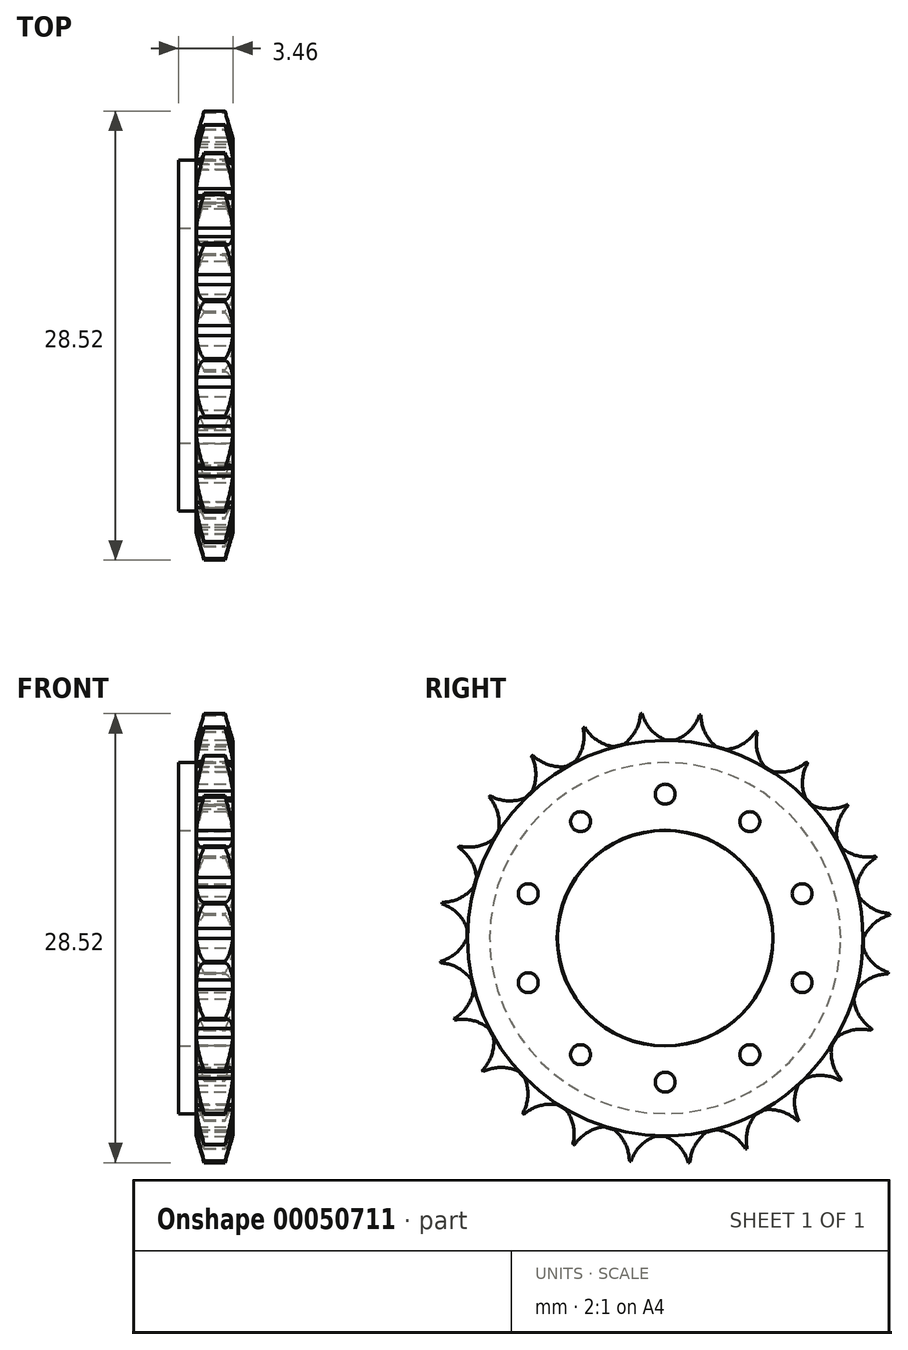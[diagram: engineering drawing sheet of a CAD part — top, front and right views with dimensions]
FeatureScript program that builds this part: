
annotation { "Feature Type Name" : "Feature", "Feature Type Description" : "" }
export const myFeature = defineFeature(function(context is Context, id is Id, definition is map)
    precondition{}
    {
        {
            var Q0;
            Q0=qCreatedBy(makeId("Right.planeOp"),FACE);
            var sketch = newSketch(context, id + "F0", { "sketchPlane" : qUnion([Q0])});
            skCircle(sketch, "E0", {"center": v(0, 0) * mm, "radius": 14.34 * mm});
            skCircle(sketch, "E1", {"center": v(0, 0) * mm, "radius": 6.86 * mm});
            skSolve(sketch);
        }
        {
            var Q0;
            Q0 = qSketchRegion(id + "F0", true);
            extrude(context, id + "F1", {"entities" : qUnion([Q0]), "flatOperationType" : FlatOperationType.REMOVE, "depth" : 2.34 * mm, "offsetDistance" : 25.4 * mm, "domain" : OperationDomain.MODEL});
        }
        {
            var Q0;
            Q0=makeQuery(id+"F1.opExtrude","CAP_EDGE",EDGE,{"disambiguationData":[OSD([sQuery(id+"F0.wireOp",EDGE,"E0")])],"isStart":false});
            var Q1;
            Q1=makeQuery(id+"F1.opExtrude","CAP_EDGE",EDGE,{"disambiguationData":[OSD([sQuery(id+"F0.wireOp",EDGE,"E0")])],"isStart":true});
            chamfer(context, id + "F2", {"entities" : qUnion([Q0, Q1]), "chamferType" : ChamferType.TWO_OFFSETS, "width1" : 1.78 * mm, "oppositeDirection" : false, "width2" : 0.5 * mm, "tangentPropagation" : true});
        }
        {
            var Q0;
            Q0=makeQuery(id+"F1.opExtrude","CAP_FACE",FACE,{"disambiguationData":[OSD([sQuery(id+"F0.wireOp",EDGE,"E0"),sQuery(id+"F0.wireOp",EDGE,"E1")])],"isStart":false});
            var sketch = newSketch(context, id + "F3", { "sketchPlane" : qUnion([Q0])});
            skCircle(sketch, "E2", {"center": v(0, 0) * mm, "radius": 12.6 * mm});
            skArc(sketch, "E3", {"start": v(-1.47, 14.28) * mm, "mid": v(-0.9, 13.23) * mm, "end": v(0.08, 12.56) * mm});
            skArc(sketch, "E4.MirrorCS", {"start": v(-1.57, 14.27) * mm, "mid": v(-1.9, 13.13) * mm, "end": v(-2.72, 12.26) * mm});
            skArc(sketch, "E5.1.0", {"start": v(-5.21, 13.38) * mm, "mid": v(-5.24, 12.19) * mm, "end": v(-5.8, 11.14) * mm});
            skArc(sketch, "E5.1.1", {"start": v(-5.12, 13.41) * mm, "mid": v(-4.3, 12.55) * mm, "end": v(-3.17, 12.15) * mm});
            skArc(sketch, "E5.2.0", {"start": v(-8.5, 11.57) * mm, "mid": v(-8.21, 10.42) * mm, "end": v(-8.49, 9.26) * mm});
            skArc(sketch, "E5.2.1", {"start": v(-8.41, 11.63) * mm, "mid": v(-7.4, 11) * mm, "end": v(-6.21, 10.92) * mm});
            skArc(sketch, "E5.3.0", {"start": v(-11.2, 8.98) * mm, "mid": v(-10.63, 7.93) * mm, "end": v(-10.6, 6.74) * mm});
            skArc(sketch, "E5.3.1", {"start": v(-11.14, 9.06) * mm, "mid": v(-10, 8.72) * mm, "end": v(-8.82, 8.94) * mm});
            skArc(sketch, "E5.4.0", {"start": v(-13.14, 5.77) * mm, "mid": v(-12.32, 4.91) * mm, "end": v(-11.98, 3.77) * mm});
            skArc(sketch, "E5.4.1", {"start": v(-13.1, 5.87) * mm, "mid": v(-11.91, 5.84) * mm, "end": v(-10.84, 6.35) * mm});
            skArc(sketch, "E5.5.0", {"start": v(-14.2, 2.18) * mm, "mid": v(-13.17, 1.56) * mm, "end": v(-12.55, 0.54) * mm});
            skArc(sketch, "E5.5.1", {"start": v(-14.17, 2.28) * mm, "mid": v(-13.02, 2.55) * mm, "end": v(-12.11, 3.33) * mm});
            skArc(sketch, "E5.6.0", {"start": v(-14.27, -1.57) * mm, "mid": v(-13.13, -1.9) * mm, "end": v(-12.26, -2.72) * mm});
            skArc(sketch, "E5.6.1", {"start": v(-14.28, -1.47) * mm, "mid": v(-13.23, -0.9) * mm, "end": v(-12.56, 0.08) * mm});
            skArc(sketch, "E5.7.0", {"start": v(-13.38, -5.21) * mm, "mid": v(-12.19, -5.24) * mm, "end": v(-11.14, -5.8) * mm});
            skArc(sketch, "E5.7.1", {"start": v(-13.41, -5.12) * mm, "mid": v(-12.55, -4.3) * mm, "end": v(-12.15, -3.17) * mm});
            skArc(sketch, "E5.8.0", {"start": v(-11.57, -8.5) * mm, "mid": v(-10.42, -8.21) * mm, "end": v(-9.26, -8.49) * mm});
            skArc(sketch, "E5.8.1", {"start": v(-11.63, -8.41) * mm, "mid": v(-11, -7.4) * mm, "end": v(-10.92, -6.21) * mm});
            skArc(sketch, "E5.9.0", {"start": v(-8.98, -11.2) * mm, "mid": v(-7.93, -10.63) * mm, "end": v(-6.74, -10.6) * mm});
            skArc(sketch, "E5.9.1", {"start": v(-9.06, -11.14) * mm, "mid": v(-8.72, -10) * mm, "end": v(-8.94, -8.82) * mm});
            skArc(sketch, "E5.10.0", {"start": v(-5.77, -13.14) * mm, "mid": v(-4.91, -12.32) * mm, "end": v(-3.77, -11.98) * mm});
            skArc(sketch, "E5.10.1", {"start": v(-5.87, -13.1) * mm, "mid": v(-5.84, -11.91) * mm, "end": v(-6.35, -10.84) * mm});
            skArc(sketch, "E5.11.0", {"start": v(-2.18, -14.2) * mm, "mid": v(-1.56, -13.17) * mm, "end": v(-0.54, -12.55) * mm});
            skArc(sketch, "E5.11.1", {"start": v(-2.28, -14.17) * mm, "mid": v(-2.55, -13.02) * mm, "end": v(-3.33, -12.11) * mm});
            skArc(sketch, "E5.12.0", {"start": v(1.57, -14.27) * mm, "mid": v(1.9, -13.13) * mm, "end": v(2.72, -12.26) * mm});
            skArc(sketch, "E5.12.1", {"start": v(1.47, -14.28) * mm, "mid": v(0.9, -13.23) * mm, "end": v(-0.08, -12.56) * mm});
            skArc(sketch, "E5.13.0", {"start": v(5.21, -13.38) * mm, "mid": v(5.24, -12.19) * mm, "end": v(5.8, -11.14) * mm});
            skArc(sketch, "E5.13.1", {"start": v(5.12, -13.41) * mm, "mid": v(4.3, -12.55) * mm, "end": v(3.17, -12.15) * mm});
            skArc(sketch, "E5.14.0", {"start": v(8.5, -11.57) * mm, "mid": v(8.21, -10.42) * mm, "end": v(8.49, -9.26) * mm});
            skArc(sketch, "E5.14.1", {"start": v(8.41, -11.63) * mm, "mid": v(7.4, -11) * mm, "end": v(6.21, -10.92) * mm});
            skArc(sketch, "E5.15.0", {"start": v(11.2, -8.98) * mm, "mid": v(10.63, -7.93) * mm, "end": v(10.6, -6.74) * mm});
            skArc(sketch, "E5.15.1", {"start": v(11.14, -9.06) * mm, "mid": v(10, -8.72) * mm, "end": v(8.82, -8.94) * mm});
            skArc(sketch, "E5.16.0", {"start": v(13.14, -5.77) * mm, "mid": v(12.32, -4.91) * mm, "end": v(11.98, -3.77) * mm});
            skArc(sketch, "E5.16.1", {"start": v(13.1, -5.87) * mm, "mid": v(11.91, -5.84) * mm, "end": v(10.84, -6.35) * mm});
            skArc(sketch, "E5.17.0", {"start": v(14.2, -2.18) * mm, "mid": v(13.17, -1.56) * mm, "end": v(12.55, -0.54) * mm});
            skArc(sketch, "E5.17.1", {"start": v(14.17, -2.28) * mm, "mid": v(13.02, -2.55) * mm, "end": v(12.11, -3.33) * mm});
            skArc(sketch, "E5.18.0", {"start": v(14.27, 1.57) * mm, "mid": v(13.13, 1.9) * mm, "end": v(12.26, 2.72) * mm});
            skArc(sketch, "E5.18.1", {"start": v(14.28, 1.47) * mm, "mid": v(13.23, 0.9) * mm, "end": v(12.56, -0.08) * mm});
            skArc(sketch, "E5.19.0", {"start": v(13.38, 5.21) * mm, "mid": v(12.19, 5.24) * mm, "end": v(11.14, 5.8) * mm});
            skArc(sketch, "E5.19.1", {"start": v(13.41, 5.12) * mm, "mid": v(12.55, 4.3) * mm, "end": v(12.15, 3.17) * mm});
            skArc(sketch, "E5.20.0", {"start": v(11.57, 8.5) * mm, "mid": v(10.42, 8.21) * mm, "end": v(9.26, 8.49) * mm});
            skArc(sketch, "E5.20.1", {"start": v(11.63, 8.41) * mm, "mid": v(11, 7.4) * mm, "end": v(10.92, 6.21) * mm});
            skArc(sketch, "E5.21.0", {"start": v(8.98, 11.2) * mm, "mid": v(7.93, 10.63) * mm, "end": v(6.74, 10.6) * mm});
            skArc(sketch, "E5.21.1", {"start": v(9.06, 11.14) * mm, "mid": v(8.72, 10) * mm, "end": v(8.94, 8.82) * mm});
            skArc(sketch, "E5.22.0", {"start": v(5.77, 13.14) * mm, "mid": v(4.91, 12.32) * mm, "end": v(3.77, 11.98) * mm});
            skArc(sketch, "E5.22.1", {"start": v(5.87, 13.1) * mm, "mid": v(5.84, 11.91) * mm, "end": v(6.35, 10.84) * mm});
            skArc(sketch, "E5.23.0", {"start": v(2.18, 14.2) * mm, "mid": v(1.56, 13.17) * mm, "end": v(0.54, 12.55) * mm});
            skArc(sketch, "E5.23.1", {"start": v(2.28, 14.17) * mm, "mid": v(2.55, 13.02) * mm, "end": v(3.33, 12.11) * mm});
            skCircle(sketch, "E6", {"center": v(0, 0) * mm, "radius": 14.36 * mm});
            skSolve(sketch);
        }
        {
            var Q0;
            {var subQ0=sQuery(id+"F3.wireOp",EDGE,"E5.18.0");var subQ1=sQuery(id+"F3.wireOp",EDGE,"E2");var subQ2=makeQuery(id+"F3.imprint","INTERSECT",VERTEX,{"derivedFrom":[subQ1,subQ0]});Q0=makeQuery(id+"F3.imprint","IMPRINT",FACE,{"disambiguationData":[TD([[makeQuery(id+"F3.imprint","IMPRINT",EDGE,{"disambiguationData":[TD([[subQ2,-1.0]])],"derivedFrom":subQ1}),-1.0]])]});}
            var Q1;
            {var subQ0=sQuery(id+"F3.wireOp",EDGE,"E5.19.0");var subQ1=sQuery(id+"F3.wireOp",EDGE,"E2");var subQ2=makeQuery(id+"F3.imprint","INTERSECT",VERTEX,{"derivedFrom":[subQ1,subQ0]});Q1=makeQuery(id+"F3.imprint","IMPRINT",FACE,{"disambiguationData":[TD([[makeQuery(id+"F3.imprint","IMPRINT",EDGE,{"disambiguationData":[TD([[subQ2,-1.0]])],"derivedFrom":subQ1}),-1.0]])]});}
            var Q2;
            {var subQ0=sQuery(id+"F3.wireOp",EDGE,"E5.20.0");var subQ1=sQuery(id+"F3.wireOp",EDGE,"E2");var subQ2=makeQuery(id+"F3.imprint","INTERSECT",VERTEX,{"derivedFrom":[subQ1,subQ0]});Q2=makeQuery(id+"F3.imprint","IMPRINT",FACE,{"disambiguationData":[TD([[makeQuery(id+"F3.imprint","IMPRINT",EDGE,{"disambiguationData":[TD([[subQ2,-1.0]])],"derivedFrom":subQ1}),-1.0]])]});}
            var Q3;
            {var subQ0=sQuery(id+"F3.wireOp",EDGE,"E5.21.0");var subQ1=sQuery(id+"F3.wireOp",EDGE,"E2");var subQ2=makeQuery(id+"F3.imprint","INTERSECT",VERTEX,{"derivedFrom":[subQ1,subQ0]});Q3=makeQuery(id+"F3.imprint","IMPRINT",FACE,{"disambiguationData":[TD([[makeQuery(id+"F3.imprint","IMPRINT",EDGE,{"disambiguationData":[TD([[subQ2,-1.0]])],"derivedFrom":subQ1}),-1.0]])]});}
            var Q4;
            {var subQ0=sQuery(id+"F3.wireOp",EDGE,"E5.22.0");var subQ1=sQuery(id+"F3.wireOp",EDGE,"E2");var subQ2=makeQuery(id+"F3.imprint","INTERSECT",VERTEX,{"derivedFrom":[subQ1,subQ0]});Q4=makeQuery(id+"F3.imprint","IMPRINT",FACE,{"disambiguationData":[TD([[makeQuery(id+"F3.imprint","IMPRINT",EDGE,{"disambiguationData":[TD([[subQ2,-1.0]])],"derivedFrom":subQ1}),-1.0]])]});}
            var Q5;
            {var subQ0=sQuery(id+"F3.wireOp",EDGE,"E5.23.0");var subQ1=sQuery(id+"F3.wireOp",EDGE,"E2");var subQ2=makeQuery(id+"F3.imprint","INTERSECT",VERTEX,{"derivedFrom":[subQ1,subQ0]});Q5=makeQuery(id+"F3.imprint","IMPRINT",FACE,{"disambiguationData":[TD([[makeQuery(id+"F3.imprint","IMPRINT",EDGE,{"disambiguationData":[TD([[subQ2,-1.0]])],"derivedFrom":subQ1}),-1.0]])]});}
            var Q6;
            {var subQ0=sQuery(id+"F3.wireOp",EDGE,"E5.1.0");var subQ1=sQuery(id+"F3.wireOp",EDGE,"E2");var subQ2=makeQuery(id+"F3.imprint","INTERSECT",VERTEX,{"derivedFrom":[subQ1,subQ0]});Q6=makeQuery(id+"F3.imprint","IMPRINT",FACE,{"disambiguationData":[TD([[makeQuery(id+"F3.imprint","IMPRINT",EDGE,{"disambiguationData":[TD([[subQ2,-1.0]])],"derivedFrom":subQ1}),-1.0]])]});}
            var Q7;
            {var subQ0=sQuery(id+"F3.wireOp",EDGE,"E5.2.0");var subQ1=sQuery(id+"F3.wireOp",EDGE,"E2");var subQ2=makeQuery(id+"F3.imprint","INTERSECT",VERTEX,{"derivedFrom":[subQ1,subQ0]});Q7=makeQuery(id+"F3.imprint","IMPRINT",FACE,{"disambiguationData":[TD([[makeQuery(id+"F3.imprint","IMPRINT",EDGE,{"disambiguationData":[TD([[subQ2,-1.0]])],"derivedFrom":subQ1}),-1.0]])]});}
            var Q8;
            {var subQ0=sQuery(id+"F3.wireOp",EDGE,"E5.3.0");var subQ1=sQuery(id+"F3.wireOp",EDGE,"E2");var subQ2=makeQuery(id+"F3.imprint","INTERSECT",VERTEX,{"derivedFrom":[subQ1,subQ0]});Q8=makeQuery(id+"F3.imprint","IMPRINT",FACE,{"disambiguationData":[TD([[makeQuery(id+"F3.imprint","IMPRINT",EDGE,{"disambiguationData":[TD([[subQ2,-1.0]])],"derivedFrom":subQ1}),-1.0]])]});}
            var Q9;
            {var subQ0=sQuery(id+"F3.wireOp",EDGE,"E5.4.0");var subQ1=sQuery(id+"F3.wireOp",EDGE,"E2");var subQ2=makeQuery(id+"F3.imprint","INTERSECT",VERTEX,{"derivedFrom":[subQ1,subQ0]});Q9=makeQuery(id+"F3.imprint","IMPRINT",FACE,{"disambiguationData":[TD([[makeQuery(id+"F3.imprint","IMPRINT",EDGE,{"disambiguationData":[TD([[subQ2,-1.0]])],"derivedFrom":subQ1}),-1.0]])]});}
            var Q10;
            {var subQ0=sQuery(id+"F3.wireOp",EDGE,"E5.5.0");var subQ1=sQuery(id+"F3.wireOp",EDGE,"E2");var subQ2=makeQuery(id+"F3.imprint","INTERSECT",VERTEX,{"derivedFrom":[subQ1,subQ0]});Q10=makeQuery(id+"F3.imprint","IMPRINT",FACE,{"disambiguationData":[TD([[makeQuery(id+"F3.imprint","IMPRINT",EDGE,{"disambiguationData":[TD([[subQ2,-1.0]])],"derivedFrom":subQ1}),-1.0]])]});}
            var Q11;
            {var subQ0=sQuery(id+"F3.wireOp",EDGE,"E5.6.0");var subQ1=sQuery(id+"F3.wireOp",EDGE,"E2");var subQ2=makeQuery(id+"F3.imprint","INTERSECT",VERTEX,{"derivedFrom":[subQ1,subQ0]});Q11=makeQuery(id+"F3.imprint","IMPRINT",FACE,{"disambiguationData":[TD([[makeQuery(id+"F3.imprint","IMPRINT",EDGE,{"disambiguationData":[TD([[subQ2,-1.0]])],"derivedFrom":subQ1}),-1.0]])]});}
            var Q12;
            {var subQ0=sQuery(id+"F3.wireOp",EDGE,"E5.7.0");var subQ1=sQuery(id+"F3.wireOp",EDGE,"E2");var subQ2=makeQuery(id+"F3.imprint","INTERSECT",VERTEX,{"derivedFrom":[subQ1,subQ0]});Q12=makeQuery(id+"F3.imprint","IMPRINT",FACE,{"disambiguationData":[TD([[makeQuery(id+"F3.imprint","IMPRINT",EDGE,{"disambiguationData":[TD([[subQ2,-1.0]])],"derivedFrom":subQ1}),-1.0]])]});}
            var Q13;
            {var subQ0=sQuery(id+"F3.wireOp",EDGE,"E5.8.0");var subQ1=sQuery(id+"F3.wireOp",EDGE,"E2");var subQ2=makeQuery(id+"F3.imprint","INTERSECT",VERTEX,{"derivedFrom":[subQ1,subQ0]});Q13=makeQuery(id+"F3.imprint","IMPRINT",FACE,{"disambiguationData":[TD([[makeQuery(id+"F3.imprint","IMPRINT",EDGE,{"disambiguationData":[TD([[subQ2,-1.0]])],"derivedFrom":subQ1}),-1.0]])]});}
            var Q14;
            {var subQ0=sQuery(id+"F3.wireOp",EDGE,"E5.9.0");var subQ1=sQuery(id+"F3.wireOp",EDGE,"E2");var subQ2=makeQuery(id+"F3.imprint","INTERSECT",VERTEX,{"derivedFrom":[subQ1,subQ0]});Q14=makeQuery(id+"F3.imprint","IMPRINT",FACE,{"disambiguationData":[TD([[makeQuery(id+"F3.imprint","IMPRINT",EDGE,{"disambiguationData":[TD([[subQ2,-1.0]])],"derivedFrom":subQ1}),-1.0]])]});}
            var Q15;
            {var subQ0=sQuery(id+"F3.wireOp",EDGE,"E5.10.0");var subQ1=sQuery(id+"F3.wireOp",EDGE,"E2");var subQ2=makeQuery(id+"F3.imprint","INTERSECT",VERTEX,{"derivedFrom":[subQ1,subQ0]});Q15=makeQuery(id+"F3.imprint","IMPRINT",FACE,{"disambiguationData":[TD([[makeQuery(id+"F3.imprint","IMPRINT",EDGE,{"disambiguationData":[TD([[subQ2,-1.0]])],"derivedFrom":subQ1}),-1.0]])]});}
            var Q16;
            {var subQ0=sQuery(id+"F3.wireOp",EDGE,"E5.11.0");var subQ1=sQuery(id+"F3.wireOp",EDGE,"E2");var subQ2=makeQuery(id+"F3.imprint","INTERSECT",VERTEX,{"derivedFrom":[subQ1,subQ0]});Q16=makeQuery(id+"F3.imprint","IMPRINT",FACE,{"disambiguationData":[TD([[makeQuery(id+"F3.imprint","IMPRINT",EDGE,{"disambiguationData":[TD([[subQ2,-1.0]])],"derivedFrom":subQ1}),-1.0]])]});}
            var Q17;
            {var subQ0=sQuery(id+"F3.wireOp",EDGE,"E5.12.0");var subQ1=sQuery(id+"F3.wireOp",EDGE,"E2");var subQ2=makeQuery(id+"F3.imprint","INTERSECT",VERTEX,{"derivedFrom":[subQ1,subQ0]});Q17=makeQuery(id+"F3.imprint","IMPRINT",FACE,{"disambiguationData":[TD([[makeQuery(id+"F3.imprint","IMPRINT",EDGE,{"disambiguationData":[TD([[subQ2,-1.0]])],"derivedFrom":subQ1}),-1.0]])]});}
            var Q18;
            {var subQ0=sQuery(id+"F3.wireOp",EDGE,"E5.13.0");var subQ1=sQuery(id+"F3.wireOp",EDGE,"E2");var subQ2=makeQuery(id+"F3.imprint","INTERSECT",VERTEX,{"derivedFrom":[subQ1,subQ0]});Q18=makeQuery(id+"F3.imprint","IMPRINT",FACE,{"disambiguationData":[TD([[makeQuery(id+"F3.imprint","IMPRINT",EDGE,{"disambiguationData":[TD([[subQ2,-1.0]])],"derivedFrom":subQ1}),-1.0]])]});}
            var Q19;
            {var subQ0=sQuery(id+"F3.wireOp",EDGE,"E5.14.0");var subQ1=sQuery(id+"F3.wireOp",EDGE,"E2");var subQ2=makeQuery(id+"F3.imprint","INTERSECT",VERTEX,{"derivedFrom":[subQ1,subQ0]});Q19=makeQuery(id+"F3.imprint","IMPRINT",FACE,{"disambiguationData":[TD([[makeQuery(id+"F3.imprint","IMPRINT",EDGE,{"disambiguationData":[TD([[subQ2,-1.0]])],"derivedFrom":subQ1}),-1.0]])]});}
            var Q20;
            {var subQ0=sQuery(id+"F3.wireOp",EDGE,"E5.15.0");var subQ1=sQuery(id+"F3.wireOp",EDGE,"E2");var subQ2=makeQuery(id+"F3.imprint","INTERSECT",VERTEX,{"derivedFrom":[subQ1,subQ0]});Q20=makeQuery(id+"F3.imprint","IMPRINT",FACE,{"disambiguationData":[TD([[makeQuery(id+"F3.imprint","IMPRINT",EDGE,{"disambiguationData":[TD([[subQ2,-1.0]])],"derivedFrom":subQ1}),-1.0]])]});}
            var Q21;
            {var subQ0=sQuery(id+"F3.wireOp",EDGE,"E5.16.0");var subQ1=sQuery(id+"F3.wireOp",EDGE,"E2");var subQ2=makeQuery(id+"F3.imprint","INTERSECT",VERTEX,{"derivedFrom":[subQ1,subQ0]});Q21=makeQuery(id+"F3.imprint","IMPRINT",FACE,{"disambiguationData":[TD([[makeQuery(id+"F3.imprint","IMPRINT",EDGE,{"disambiguationData":[TD([[subQ2,-1.0]])],"derivedFrom":subQ1}),-1.0]])]});}
            var Q22;
            {var subQ0=sQuery(id+"F3.wireOp",EDGE,"E5.18.1");var subQ1=sQuery(id+"F3.wireOp",EDGE,"E2");var subQ2=makeQuery(id+"F3.imprint","INTERSECT",VERTEX,{"derivedFrom":[subQ1,subQ0]});Q22=makeQuery(id+"F3.imprint","IMPRINT",FACE,{"disambiguationData":[TD([[makeQuery(id+"F3.imprint","IMPRINT",EDGE,{"disambiguationData":[TD([[subQ2,1.0]])],"derivedFrom":subQ1}),-1.0]])]});}
            var Q23;
            {var subQ0=sQuery(id+"F3.wireOp",EDGE,"E4.MirrorCS");var subQ1=sQuery(id+"F3.wireOp",EDGE,"E2");var subQ2=makeQuery(id+"F3.imprint","INTERSECT",VERTEX,{"derivedFrom":[subQ1,subQ0]});Q23=makeQuery(id+"F3.imprint","IMPRINT",FACE,{"disambiguationData":[TD([[makeQuery(id+"F3.imprint","IMPRINT",EDGE,{"disambiguationData":[TD([[subQ2,-1.0]])],"derivedFrom":subQ1}),-1.0]])]});}
            extrude(context, id + "F4", {"entities" : qUnion([Q0, Q1, Q2, Q3, Q4, Q5, Q6, Q7, Q8, Q9, Q10, Q11, Q12, Q13, Q14, Q15, Q16, Q17, Q18, Q19, Q20, Q21, Q22, Q23]), "operationType" : NewBodyOperationType.REMOVE, "flatOperationType" : FlatOperationType.REMOVE, "oppositeDirection" : true, "depth" : 25.4 * mm, "offsetDistance" : 25.4 * mm, "domain" : OperationDomain.MODEL});
        }
        {
            var Q0;
            Q0=makeQuery(id+"F1.opExtrude","CAP_FACE",FACE,{"disambiguationData":[OSD([sQuery(id+"F0.wireOp",EDGE,"E0"),sQuery(id+"F0.wireOp",EDGE,"E1")])],"isStart":false});
            var sketch = newSketch(context, id + "F5", { "sketchPlane" : qUnion([Q0])});
            skCircle(sketch, "E7", {"center": v(0, -9.15) * mm, "radius": 0.63 * mm});
            skCircle(sketch, "E8.1.0", {"center": v(5.38, -7.4) * mm, "radius": 0.63 * mm});
            skCircle(sketch, "E8.2.0", {"center": v(8.7, -2.83) * mm, "radius": 0.63 * mm});
            skCircle(sketch, "E8.3.0", {"center": v(8.7, 2.83) * mm, "radius": 0.63 * mm});
            skCircle(sketch, "E8.4.0", {"center": v(5.38, 7.4) * mm, "radius": 0.63 * mm});
            skCircle(sketch, "E8.5.0", {"center": v(0, 9.15) * mm, "radius": 0.63 * mm});
            skCircle(sketch, "E8.6.0", {"center": v(-5.38, 7.4) * mm, "radius": 0.63 * mm});
            skCircle(sketch, "E8.7.0", {"center": v(-8.7, 2.83) * mm, "radius": 0.63 * mm});
            skCircle(sketch, "E8.8.0", {"center": v(-8.7, -2.83) * mm, "radius": 0.63 * mm});
            skCircle(sketch, "E8.9.0", {"center": v(-5.38, -7.4) * mm, "radius": 0.63 * mm});
            skPoint(sketch, "E8.center", {"position": v(0, 0) * mm});
            skSolve(sketch);
        }
        {
            var Q0;
            Q0 = qSketchRegion(id + "F5", true);
            extrude(context, id + "F6", {"entities" : qUnion([Q0]), "operationType" : NewBodyOperationType.REMOVE, "oppositeDirection" : true, "depth" : 25.4 * mm});
        }
        {
            var Q0;
            Q0=qCreatedBy(makeId("Right.planeOp"),FACE);
            var sketch = newSketch(context, id + "F7", { "sketchPlane" : qUnion([Q0])});
            skCircle(sketch, "E9", {"center": v(0, 0) * mm, "radius": 11.15 * mm});
            skCircle(sketch, "E10", {"center": v(0, 0) * mm, "radius": 6.83 * mm});
            skSolve(sketch);
        }
        {
            var Q0;
            Q0 = qSketchRegion(id + "F7", true);
            extrude(context, id + "F8", {"entities" : qUnion([Q0]), "operationType" : NewBodyOperationType.ADD, "oppositeDirection" : true, "depth" : 1.12 * mm});
        }
    });
